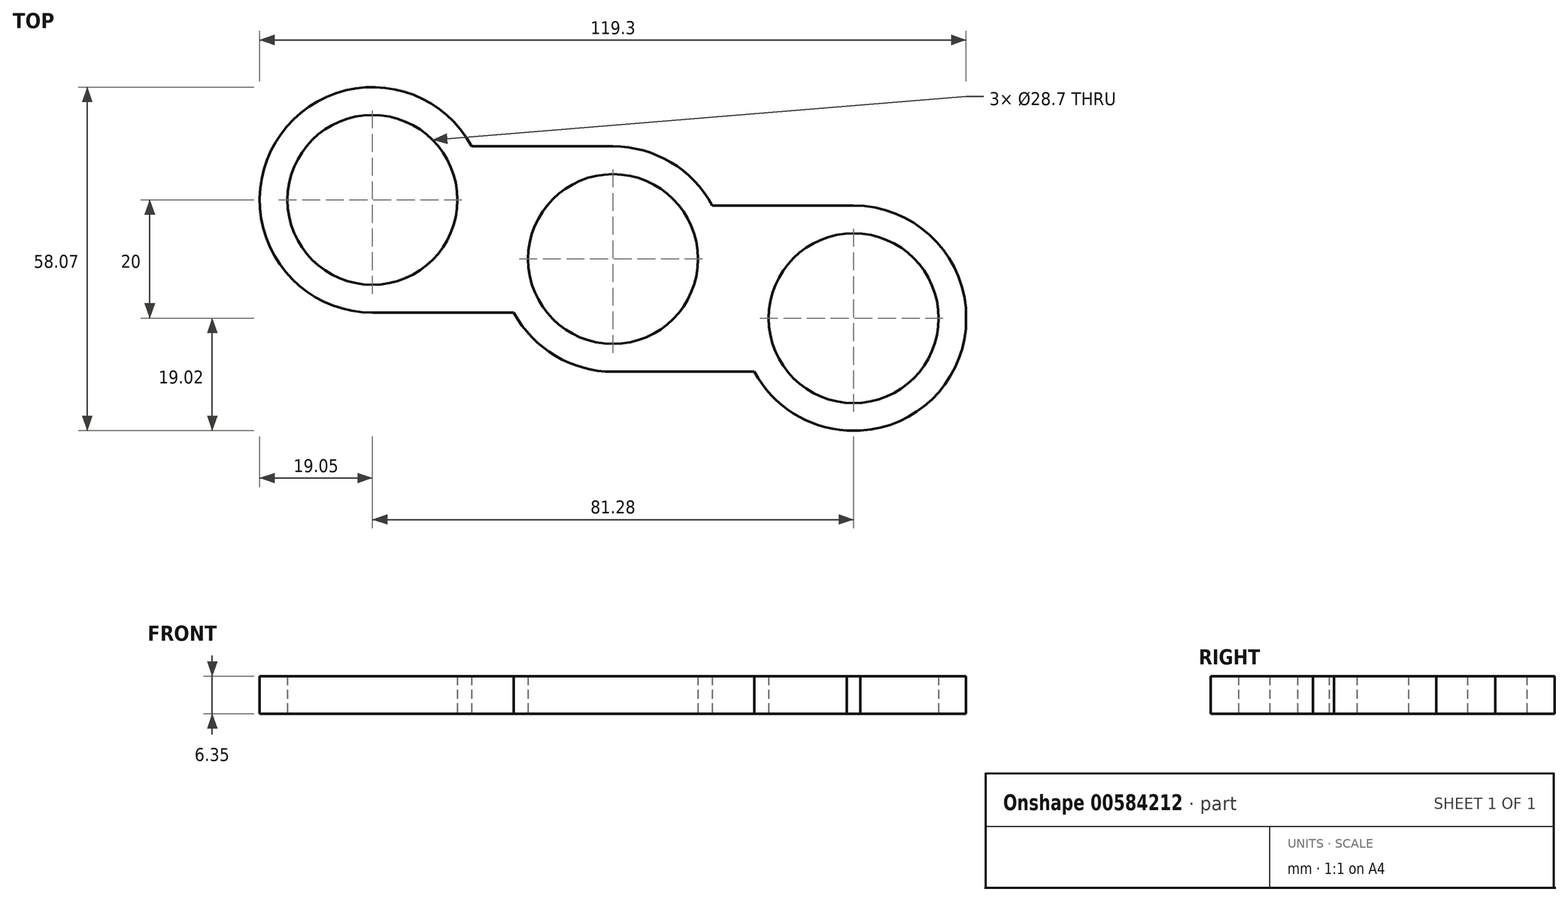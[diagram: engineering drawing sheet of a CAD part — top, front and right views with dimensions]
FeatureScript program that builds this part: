
annotation { "Feature Type Name" : "Feature", "Feature Type Description" : "" }
export const myFeature = defineFeature(function(context is Context, id is Id, definition is map)
    precondition{}
    {
        {
            var Q0;
            Q0=qCreatedBy(makeId("Top.planeOp"),FACE);
            var sketch = newSketch(context, id + "F0", { "sketchPlane" : qUnion([Q0])});
            skCircle(sketch, "E0", {"center": v(0, 0) * mm, "radius": 14.35 * mm});
            skCircle(sketch, "E1", {"center": v(40.64, -10) * mm, "radius": 14.35 * mm});
            skCircle(sketch, "E2", {"center": v(-40.64, 10) * mm, "radius": 14.35 * mm});
            skCircle(sketch, "E3", {"center": v(-40.64, 10) * mm, "radius": 19.05 * mm});
            skCircle(sketch, "E4", {"center": v(0, 0) * mm, "radius": 19.05 * mm});
            skCircle(sketch, "E5", {"center": v(40.64, -10) * mm, "radius": 19.05 * mm});
            skLineSegment(sketch, "E6", {"start": v(0, 19.05) * mm, "end": v(-23.88, 19.05) * mm});
            skLineSegment(sketch, "E7", {"start": v(-40.64, -9.05) * mm, "end": v(-16.76, -9.05) * mm});
            skLineSegment(sketch, "E8", {"start": v(0, -19.05) * mm, "end": v(23.88, -19.05) * mm});
            skLineSegment(sketch, "E9", {"start": v(40.64, 9.05) * mm, "end": v(16.76, 9.05) * mm});
            skLineSegment(sketch, "E10", {"start": v(-59.69, 10.15) * mm, "end": v(-59.69, 55.41) * mm});
            skLineSegment(sketch, "E11", {"start": v(59.6, -11.8) * mm, "end": v(59.6, 49.87) * mm});
            skLineSegment(sketch, "E12", {"start": v(-40.64, 29.05) * mm, "end": v(-1.94, 29.05) * mm});
            skLineSegment(sketch, "E13", {"start": v(41.8, -29.02) * mm, "end": v(-19.86, -29.02) * mm});
            skSolve(sketch);
        }
        {
            var Q0;
            Q0=makeQuery(id+"F0.imprint","IMPRINT",FACE,{"disambiguationData":[TD([[makeQuery(id+"F0.imprint","IMPRINT",EDGE,{"derivedFrom":sQuery(id+"F0.wireOp",EDGE,"E2")}),-1.0]])]});
            var Q1;
            {var subQ0=sQuery(id+"F0.wireOp",EDGE,"E6");Q1=makeQuery(id+"F0.imprint","IMPRINT",FACE,{"disambiguationData":[TD([[makeQuery(id+"F0.imprint","IMPRINT",EDGE,{"derivedFrom":subQ0}),1.0]])]});}
            var Q2;
            Q2=makeQuery(id+"F0.imprint","IMPRINT",FACE,{"disambiguationData":[TD([[makeQuery(id+"F0.imprint","IMPRINT",EDGE,{"derivedFrom":sQuery(id+"F0.wireOp",EDGE,"E0")}),-1.0]])]});
            var Q3;
            {var subQ0=sQuery(id+"F0.wireOp",EDGE,"E8");Q3=makeQuery(id+"F0.imprint","IMPRINT",FACE,{"disambiguationData":[TD([[makeQuery(id+"F0.imprint","IMPRINT",EDGE,{"derivedFrom":subQ0}),1.0]])]});}
            var Q4;
            Q4=makeQuery(id+"F0.imprint","IMPRINT",FACE,{"disambiguationData":[TD([[makeQuery(id+"F0.imprint","IMPRINT",EDGE,{"derivedFrom":sQuery(id+"F0.wireOp",EDGE,"E1")}),-1.0]])]});
            extrude(context, id + "F1", {"entities" : qUnion([Q0, Q1, Q2, Q3, Q4]), "depth" : 6.35 * mm, "offsetDistance" : 25.4 * mm});
        }
    });
